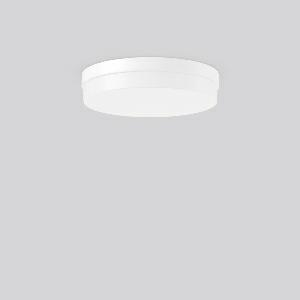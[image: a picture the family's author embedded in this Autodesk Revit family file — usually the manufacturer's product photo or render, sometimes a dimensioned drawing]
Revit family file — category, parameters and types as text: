
# Revit family: flat_kreis_221156_002_1_f20c
name_source: partatom
category: Lighting Fixtures
units: mm (PartAtom-declared; Revit-internal decimal feet)

## family parameters
Cut with Voids When Loaded = No
Host = Face
Light Source = No
Part Type = Normal
Room Calculation Point = No
Round Connector Dimension = Use Diameter
Shared = No

## types (1)
- FLAT KREIS (1 x LED Modul 840, 1300 lm, 4000)
    Apparent Load = 19 VA
    CIE Flux Codes = 42 73 92 90 100
    Color Rendering = 80
    Color Temperature = 4000
    Default Elevation = 1800 mm
    Description = Series: FLAT KREIS
Decorative round surface-mounted luminaire. Base: plastic. Diffuser: plastic (polypropylene), opal. Diffuser fastening: spring system. Homogeneous and smooth light distribution. 
Colour: white
Diameter: 380 mm
Height: 78 mm
Lamp: LED exchangeable
Socket: without socket
Colour temperature: 4000K
Colour rendering index (CRI): 83
System power: 19 W
Rated luminous flux: 1300 lm
Beam angle Down: 121°
Luminous efficiency: 68 lm/W
Control gear: AC Strom, dim.Ph.an-/abschnitt
Protection class: I
Type of protection: IP 43
    Height = 78 mm  [stored 0.255906 ft]
    Lamp = 1 x LED Modul 840
    Lamp Light Flux = 1300 lm
    Lamp count = 1
    Length = 380 mm
    Lifetime = 50000 h
    Luminous efficacy = 68 lm/W
    Manufacturer = RZB
    ModVariant = No
    Model = 221156.002.1
    Mounting Place = Ceiling, Wall
    Mounting Type = Surface mounted
    Number of Poles = 1
    OnlyDefault = Yes
    Power Factor = 1
    Product Name = FLAT KREIS
    Product group = Surface mounted ceiling and wall luminaires
    ProductGroupID = 305
    Protection Class = Protection class I
    Protection Degree = IP 43
    RLX_Detail_Level = 1
    RLX_Emergency_Light_Flux = 0 lm
    RLX_Emergency_Type = 0
    RLX_Emergency_Type_DB = No
    RlxData = <blob elided: 12841 chars, md5=eaca357f>
    Socket = socket
    Standby Power = 0 W
    System Light Flux = 1300 lm
    System Power = 19 W
    Type Comments = ALEA SPOT
    Type Image = 221062.862.79.jpg
    URL = http://relux.com
    VarID = ---
    Voltage = 230 V
    Voltage Range = 220-240 V
    Weight = 0.00 kg
    Width = 0 mm  [stored 0 ft]

note: [stored X ft] marks values corroborated as IEEE doubles in the binary element streams (Revit-internal decimal feet)

## geometry (parser evidence)
native form markers: Sweep x10
no freeform markers — native parametric forms only
